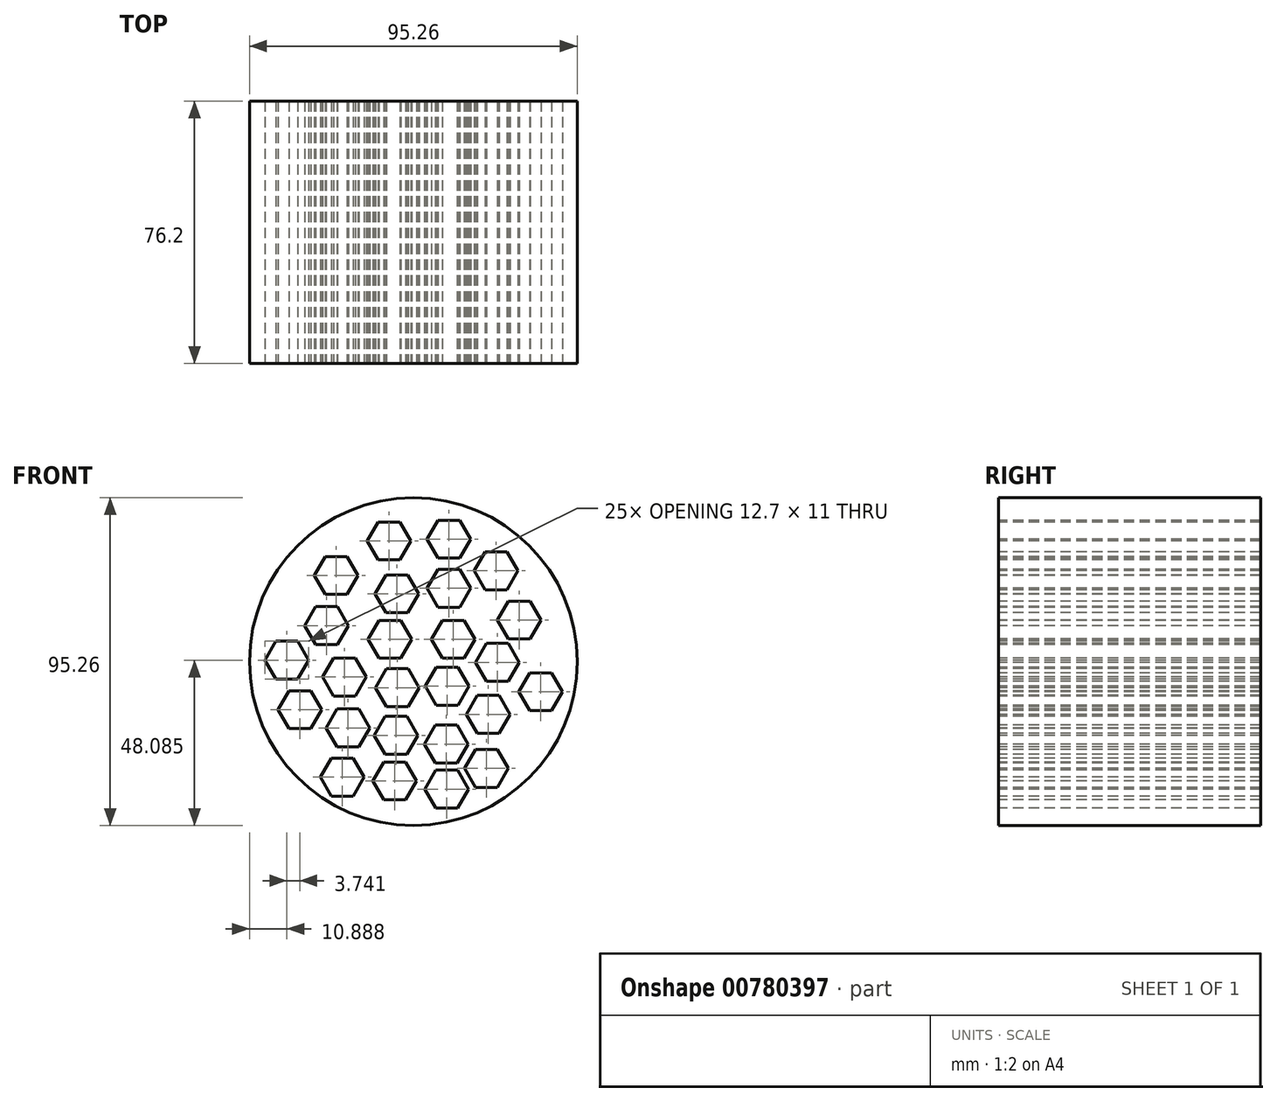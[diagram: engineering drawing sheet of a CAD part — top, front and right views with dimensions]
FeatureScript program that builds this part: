
annotation { "Feature Type Name" : "Feature", "Feature Type Description" : "" }
export const myFeature = defineFeature(function(context is Context, id is Id, definition is map)
    precondition{}
    {
        {
            var Q0;
            Q0=qCreatedBy(makeId("Front.planeOp"),FACE);
            var sketch = newSketch(context, id + "F0", { "sketchPlane" : qUnion([Q0])});
            skCircle(sketch, "E0", {"center": v(0, 0) * mm, "radius": 47.63 * mm});
            skSolve(sketch);
        }
        {
            var Q0;
            Q0=makeQuery(id+"F0.imprint","IMPRINT",FACE,{"disambiguationData":[TD([[makeQuery(id+"F0.imprint","IMPRINT",EDGE,{"derivedFrom":sQuery(id+"F0.wireOp",EDGE,"E0")}),1.0]])]});
            extrude(context, id + "F1", {"entities" : qUnion([Q0]), "depth" : 76.2 * mm, "offsetDistance" : 25.4 * mm});
        }
        {
            var Q0;
            Q0=makeQuery(id+"F1.opExtrude","CAP_FACE",FACE,{"disambiguationData":[OSD([sQuery(id+"F0.wireOp",EDGE,"E0")])],"isStart":false});
            var sketch = newSketch(context, id + "F2", { "sketchPlane" : qUnion([Q0])});
            skCircle(sketch, "E1.cCircle", {"center": v(-22.42, 25.02) * mm, "radius": 5.5 * mm, "construction": true});
            skLineSegment(sketch, "E1.0", {"start": v(-19.25, 30.52) * mm, "end": v(-16.07, 25.02) * mm});
            skLineSegment(sketch, "E1.1", {"start": v(-16.07, 25.02) * mm, "end": v(-19.25, 19.52) * mm});
            skLineSegment(sketch, "E1.2", {"start": v(-19.25, 19.52) * mm, "end": v(-25.6, 19.52) * mm});
            skLineSegment(sketch, "E1.3", {"start": v(-25.6, 19.52) * mm, "end": v(-28.77, 25.02) * mm});
            skLineSegment(sketch, "E1.4", {"start": v(-28.77, 25.02) * mm, "end": v(-25.6, 30.52) * mm});
            skLineSegment(sketch, "E1.5", {"start": v(-25.6, 30.52) * mm, "end": v(-19.25, 30.52) * mm});
            skPoint(sketch, "E1.0.midPoint", {"position": v(-17.66, 27.77) * mm});
            skCircle(sketch, "E2.cCircle", {"center": v(-7.08, 35.06) * mm, "radius": 5.5 * mm, "construction": true});
            skLineSegment(sketch, "E2.0", {"start": v(-3.9, 40.56) * mm, "end": v(-0.73, 35.06) * mm});
            skLineSegment(sketch, "E2.1", {"start": v(-0.73, 35.06) * mm, "end": v(-3.9, 29.56) * mm});
            skLineSegment(sketch, "E2.2", {"start": v(-3.9, 29.56) * mm, "end": v(-10.26, 29.56) * mm});
            skLineSegment(sketch, "E2.3", {"start": v(-10.26, 29.56) * mm, "end": v(-13.43, 35.06) * mm});
            skLineSegment(sketch, "E2.4", {"start": v(-13.43, 35.06) * mm, "end": v(-10.26, 40.56) * mm});
            skLineSegment(sketch, "E2.5", {"start": v(-10.26, 40.56) * mm, "end": v(-3.9, 40.56) * mm});
            skPoint(sketch, "E2.0.midPoint", {"position": v(-2.32, 37.8) * mm});
            skCircle(sketch, "E3.cCircle", {"center": v(10.28, 35.6) * mm, "radius": 5.5 * mm, "construction": true});
            skLineSegment(sketch, "E3.0", {"start": v(13.46, 41.09) * mm, "end": v(16.63, 35.6) * mm});
            skLineSegment(sketch, "E3.1", {"start": v(16.63, 35.6) * mm, "end": v(13.46, 30.1) * mm});
            skLineSegment(sketch, "E3.2", {"start": v(13.46, 30.1) * mm, "end": v(7.1, 30.1) * mm});
            skLineSegment(sketch, "E3.3", {"start": v(7.1, 30.1) * mm, "end": v(3.93, 35.6) * mm});
            skLineSegment(sketch, "E3.4", {"start": v(3.93, 35.6) * mm, "end": v(7.1, 41.09) * mm});
            skLineSegment(sketch, "E3.5", {"start": v(7.1, 41.09) * mm, "end": v(13.46, 41.09) * mm});
            skPoint(sketch, "E3.0.midPoint", {"position": v(15.05, 38.34) * mm});
            skCircle(sketch, "E4.cCircle", {"center": v(-4.81, 19.7) * mm, "radius": 5.5 * mm, "construction": true});
            skLineSegment(sketch, "E4.0", {"start": v(-1.64, 25.2) * mm, "end": v(1.54, 19.7) * mm});
            skLineSegment(sketch, "E4.1", {"start": v(1.54, 19.7) * mm, "end": v(-1.64, 14.2) * mm});
            skLineSegment(sketch, "E4.2", {"start": v(-1.64, 14.2) * mm, "end": v(-7.99, 14.2) * mm});
            skLineSegment(sketch, "E4.3", {"start": v(-7.99, 14.2) * mm, "end": v(-11.16, 19.7) * mm});
            skLineSegment(sketch, "E4.4", {"start": v(-11.16, 19.7) * mm, "end": v(-7.99, 25.2) * mm});
            skLineSegment(sketch, "E4.5", {"start": v(-7.99, 25.2) * mm, "end": v(-1.64, 25.2) * mm});
            skPoint(sketch, "E4.0.midPoint", {"position": v(-0.05, 22.44) * mm});
            skCircle(sketch, "E5.cCircle", {"center": v(10.28, 21.3) * mm, "radius": 5.5 * mm, "construction": true});
            skLineSegment(sketch, "E5.0", {"start": v(13.46, 26.8) * mm, "end": v(16.63, 21.3) * mm});
            skLineSegment(sketch, "E5.1", {"start": v(16.63, 21.3) * mm, "end": v(13.46, 15.8) * mm});
            skLineSegment(sketch, "E5.2", {"start": v(13.46, 15.8) * mm, "end": v(7.1, 15.8) * mm});
            skLineSegment(sketch, "E5.3", {"start": v(7.1, 15.8) * mm, "end": v(3.93, 21.3) * mm});
            skLineSegment(sketch, "E5.4", {"start": v(3.93, 21.3) * mm, "end": v(7.1, 26.8) * mm});
            skLineSegment(sketch, "E5.5", {"start": v(7.1, 26.8) * mm, "end": v(13.46, 26.8) * mm});
            skPoint(sketch, "E5.0.midPoint", {"position": v(15.05, 24.05) * mm});
            skCircle(sketch, "E6.cCircle", {"center": v(24.04, 26.37) * mm, "radius": 5.5 * mm, "construction": true});
            skLineSegment(sketch, "E6.0", {"start": v(27.22, 31.87) * mm, "end": v(30.4, 26.37) * mm});
            skLineSegment(sketch, "E6.1", {"start": v(30.4, 26.37) * mm, "end": v(27.22, 20.87) * mm});
            skLineSegment(sketch, "E6.2", {"start": v(27.22, 20.87) * mm, "end": v(20.87, 20.87) * mm});
            skLineSegment(sketch, "E6.3", {"start": v(20.87, 20.87) * mm, "end": v(17.7, 26.37) * mm});
            skLineSegment(sketch, "E6.4", {"start": v(17.7, 26.37) * mm, "end": v(20.87, 31.87) * mm});
            skLineSegment(sketch, "E6.5", {"start": v(20.87, 31.87) * mm, "end": v(27.22, 31.87) * mm});
            skPoint(sketch, "E6.0.midPoint", {"position": v(28.8, 29.12) * mm});
            skCircle(sketch, "E7.cCircle", {"center": v(30.72, 12.08) * mm, "radius": 5.5 * mm, "construction": true});
            skLineSegment(sketch, "E7.0", {"start": v(33.9, 17.58) * mm, "end": v(37.07, 12.08) * mm});
            skLineSegment(sketch, "E7.1", {"start": v(37.07, 12.08) * mm, "end": v(33.9, 6.58) * mm});
            skLineSegment(sketch, "E7.2", {"start": v(33.9, 6.58) * mm, "end": v(27.55, 6.58) * mm});
            skLineSegment(sketch, "E7.3", {"start": v(27.55, 6.58) * mm, "end": v(24.37, 12.08) * mm});
            skLineSegment(sketch, "E7.4", {"start": v(24.37, 12.08) * mm, "end": v(27.55, 17.58) * mm});
            skLineSegment(sketch, "E7.5", {"start": v(27.55, 17.58) * mm, "end": v(33.9, 17.58) * mm});
            skPoint(sketch, "E7.0.midPoint", {"position": v(35.49, 14.83) * mm});
            skCircle(sketch, "E8.cCircle", {"center": v(11.62, 6.47) * mm, "radius": 5.5 * mm, "construction": true});
            skLineSegment(sketch, "E8.0", {"start": v(14.8, 11.97) * mm, "end": v(17.97, 6.47) * mm});
            skLineSegment(sketch, "E8.1", {"start": v(17.97, 6.47) * mm, "end": v(14.8, 0.97) * mm});
            skLineSegment(sketch, "E8.2", {"start": v(14.8, 0.97) * mm, "end": v(8.44, 0.97) * mm});
            skLineSegment(sketch, "E8.3", {"start": v(8.44, 0.97) * mm, "end": v(5.27, 6.47) * mm});
            skLineSegment(sketch, "E8.4", {"start": v(5.27, 6.47) * mm, "end": v(8.44, 11.97) * mm});
            skLineSegment(sketch, "E8.5", {"start": v(8.44, 11.97) * mm, "end": v(14.8, 11.97) * mm});
            skPoint(sketch, "E8.0.midPoint", {"position": v(16.38, 9.22) * mm});
            skCircle(sketch, "E9.cCircle", {"center": v(-6.82, 6.47) * mm, "radius": 5.5 * mm, "construction": true});
            skLineSegment(sketch, "E9.0", {"start": v(-3.64, 11.97) * mm, "end": v(-0.47, 6.47) * mm});
            skLineSegment(sketch, "E9.1", {"start": v(-0.47, 6.47) * mm, "end": v(-3.64, 0.97) * mm});
            skLineSegment(sketch, "E9.2", {"start": v(-3.64, 0.97) * mm, "end": v(-10, 0.97) * mm});
            skLineSegment(sketch, "E9.3", {"start": v(-10, 0.97) * mm, "end": v(-13.17, 6.47) * mm});
            skLineSegment(sketch, "E9.4", {"start": v(-13.17, 6.47) * mm, "end": v(-10, 11.97) * mm});
            skLineSegment(sketch, "E9.5", {"start": v(-10, 11.97) * mm, "end": v(-3.64, 11.97) * mm});
            skPoint(sketch, "E9.0.midPoint", {"position": v(-2.05, 9.22) * mm});
            skCircle(sketch, "E10.cCircle", {"center": v(-25.25, 10.47) * mm, "radius": 5.5 * mm, "construction": true});
            skLineSegment(sketch, "E10.0", {"start": v(-22.08, 15.97) * mm, "end": v(-18.9, 10.47) * mm});
            skLineSegment(sketch, "E10.1", {"start": v(-18.9, 10.47) * mm, "end": v(-22.08, 4.98) * mm});
            skLineSegment(sketch, "E10.2", {"start": v(-22.08, 4.98) * mm, "end": v(-28.43, 4.98) * mm});
            skLineSegment(sketch, "E10.3", {"start": v(-28.43, 4.98) * mm, "end": v(-31.6, 10.47) * mm});
            skLineSegment(sketch, "E10.4", {"start": v(-31.6, 10.47) * mm, "end": v(-28.43, 15.97) * mm});
            skLineSegment(sketch, "E10.5", {"start": v(-28.43, 15.97) * mm, "end": v(-22.08, 15.97) * mm});
            skPoint(sketch, "E10.0.midPoint", {"position": v(-20.5, 13.22) * mm});
            skCircle(sketch, "E11.cCircle", {"center": v(-36.74, 0.46) * mm, "radius": 5.5 * mm, "construction": true});
            skLineSegment(sketch, "E11.0", {"start": v(-33.57, 5.95) * mm, "end": v(-30.4, 0.46) * mm});
            skLineSegment(sketch, "E11.1", {"start": v(-30.4, 0.46) * mm, "end": v(-33.57, -5.04) * mm});
            skLineSegment(sketch, "E11.2", {"start": v(-33.57, -5.04) * mm, "end": v(-39.92, -5.04) * mm});
            skLineSegment(sketch, "E11.3", {"start": v(-39.92, -5.04) * mm, "end": v(-43.1, 0.46) * mm});
            skLineSegment(sketch, "E11.4", {"start": v(-43.1, 0.46) * mm, "end": v(-39.92, 5.95) * mm});
            skLineSegment(sketch, "E11.5", {"start": v(-39.92, 5.95) * mm, "end": v(-33.57, 5.95) * mm});
            skPoint(sketch, "E11.0.midPoint", {"position": v(-31.98, 3.2) * mm});
            skCircle(sketch, "E12.cCircle", {"center": v(-33, -13.97) * mm, "radius": 5.5 * mm, "construction": true});
            skLineSegment(sketch, "E12.0", {"start": v(-29.83, -8.47) * mm, "end": v(-26.65, -13.97) * mm});
            skLineSegment(sketch, "E12.1", {"start": v(-26.65, -13.97) * mm, "end": v(-29.83, -19.47) * mm});
            skLineSegment(sketch, "E12.2", {"start": v(-29.83, -19.47) * mm, "end": v(-36.18, -19.47) * mm});
            skLineSegment(sketch, "E12.3", {"start": v(-36.18, -19.47) * mm, "end": v(-39.35, -13.97) * mm});
            skLineSegment(sketch, "E12.4", {"start": v(-39.35, -13.97) * mm, "end": v(-36.18, -8.47) * mm});
            skLineSegment(sketch, "E12.5", {"start": v(-36.18, -8.47) * mm, "end": v(-29.83, -8.47) * mm});
            skPoint(sketch, "E12.0.midPoint", {"position": v(-28.24, -11.22) * mm});
            skCircle(sketch, "E13.cCircle", {"center": v(-20.04, -4.49) * mm, "radius": 5.5 * mm, "construction": true});
            skLineSegment(sketch, "E13.0", {"start": v(-16.87, 1.01) * mm, "end": v(-13.7, -4.49) * mm});
            skLineSegment(sketch, "E13.1", {"start": v(-13.7, -4.49) * mm, "end": v(-16.87, -9.99) * mm});
            skLineSegment(sketch, "E13.2", {"start": v(-16.87, -9.99) * mm, "end": v(-23.22, -9.99) * mm});
            skLineSegment(sketch, "E13.3", {"start": v(-23.22, -9.99) * mm, "end": v(-26.4, -4.49) * mm});
            skLineSegment(sketch, "E13.4", {"start": v(-26.4, -4.49) * mm, "end": v(-23.22, 1.01) * mm});
            skLineSegment(sketch, "E13.5", {"start": v(-23.22, 1.01) * mm, "end": v(-16.87, 1.01) * mm});
            skPoint(sketch, "E13.0.midPoint", {"position": v(-15.28, -1.74) * mm});
            skCircle(sketch, "E14.cCircle", {"center": v(-4.68, -7.56) * mm, "radius": 5.5 * mm, "construction": true});
            skLineSegment(sketch, "E14.0", {"start": v(-1.5, -2.06) * mm, "end": v(1.67, -7.56) * mm});
            skLineSegment(sketch, "E14.1", {"start": v(1.67, -7.56) * mm, "end": v(-1.5, -13.06) * mm});
            skLineSegment(sketch, "E14.2", {"start": v(-1.5, -13.06) * mm, "end": v(-7.85, -13.06) * mm});
            skLineSegment(sketch, "E14.3", {"start": v(-7.85, -13.06) * mm, "end": v(-11.03, -7.56) * mm});
            skLineSegment(sketch, "E14.4", {"start": v(-11.03, -7.56) * mm, "end": v(-7.85, -2.06) * mm});
            skLineSegment(sketch, "E14.5", {"start": v(-7.85, -2.06) * mm, "end": v(-1.5, -2.06) * mm});
            skPoint(sketch, "E14.0.midPoint", {"position": v(0.08, -4.81) * mm});
            skCircle(sketch, "E15.cCircle", {"center": v(9.75, -7.16) * mm, "radius": 5.5 * mm, "construction": true});
            skLineSegment(sketch, "E15.0", {"start": v(12.92, -1.66) * mm, "end": v(16.1, -7.16) * mm});
            skLineSegment(sketch, "E15.1", {"start": v(16.1, -7.16) * mm, "end": v(12.92, -12.66) * mm});
            skLineSegment(sketch, "E15.2", {"start": v(12.92, -12.66) * mm, "end": v(6.57, -12.66) * mm});
            skLineSegment(sketch, "E15.3", {"start": v(6.57, -12.66) * mm, "end": v(3.4, -7.16) * mm});
            skLineSegment(sketch, "E15.4", {"start": v(3.4, -7.16) * mm, "end": v(6.57, -1.66) * mm});
            skLineSegment(sketch, "E15.5", {"start": v(6.57, -1.66) * mm, "end": v(12.92, -1.66) * mm});
            skPoint(sketch, "E15.0.midPoint", {"position": v(14.51, -4.4) * mm});
            skCircle(sketch, "E16.cCircle", {"center": v(24.44, -0.21) * mm, "radius": 5.5 * mm, "construction": true});
            skLineSegment(sketch, "E16.0", {"start": v(27.62, 5.29) * mm, "end": v(30.8, -0.21) * mm});
            skLineSegment(sketch, "E16.1", {"start": v(30.8, -0.21) * mm, "end": v(27.62, -5.71) * mm});
            skLineSegment(sketch, "E16.2", {"start": v(27.62, -5.71) * mm, "end": v(21.27, -5.71) * mm});
            skLineSegment(sketch, "E16.3", {"start": v(21.27, -5.71) * mm, "end": v(18.1, -0.21) * mm});
            skLineSegment(sketch, "E16.4", {"start": v(18.1, -0.21) * mm, "end": v(21.27, 5.29) * mm});
            skLineSegment(sketch, "E16.5", {"start": v(21.27, 5.29) * mm, "end": v(27.62, 5.29) * mm});
            skPoint(sketch, "E16.0.midPoint", {"position": v(29.2, 2.54) * mm});
            skCircle(sketch, "E17.cCircle", {"center": v(37, -8.76) * mm, "radius": 5.5 * mm, "construction": true});
            skLineSegment(sketch, "E17.0", {"start": v(40.18, -3.26) * mm, "end": v(43.35, -8.76) * mm});
            skLineSegment(sketch, "E17.1", {"start": v(43.35, -8.76) * mm, "end": v(40.18, -14.26) * mm});
            skLineSegment(sketch, "E17.2", {"start": v(40.18, -14.26) * mm, "end": v(33.83, -14.26) * mm});
            skLineSegment(sketch, "E17.3", {"start": v(33.83, -14.26) * mm, "end": v(30.65, -8.76) * mm});
            skLineSegment(sketch, "E17.4", {"start": v(30.65, -8.76) * mm, "end": v(33.83, -3.26) * mm});
            skLineSegment(sketch, "E17.5", {"start": v(33.83, -3.26) * mm, "end": v(40.18, -3.26) * mm});
            skPoint(sketch, "E17.0.midPoint", {"position": v(41.76, -6.01) * mm});
            skCircle(sketch, "E18.cCircle", {"center": v(21.77, -15.3) * mm, "radius": 5.5 * mm, "construction": true});
            skLineSegment(sketch, "E18.0", {"start": v(24.95, -9.8) * mm, "end": v(28.12, -15.3) * mm});
            skLineSegment(sketch, "E18.1", {"start": v(28.12, -15.3) * mm, "end": v(24.95, -20.8) * mm});
            skLineSegment(sketch, "E18.2", {"start": v(24.95, -20.8) * mm, "end": v(18.6, -20.8) * mm});
            skLineSegment(sketch, "E18.3", {"start": v(18.6, -20.8) * mm, "end": v(15.42, -15.3) * mm});
            skLineSegment(sketch, "E18.4", {"start": v(15.42, -15.3) * mm, "end": v(18.6, -9.8) * mm});
            skLineSegment(sketch, "E18.5", {"start": v(18.6, -9.8) * mm, "end": v(24.95, -9.8) * mm});
            skPoint(sketch, "E18.0.midPoint", {"position": v(26.53, -12.56) * mm});
            skCircle(sketch, "E19.cCircle", {"center": v(-19.04, -19.26) * mm, "radius": 5.5 * mm, "construction": true});
            skLineSegment(sketch, "E19.0", {"start": v(-15.86, -13.76) * mm, "end": v(-12.69, -19.26) * mm});
            skLineSegment(sketch, "E19.1", {"start": v(-12.69, -19.26) * mm, "end": v(-15.86, -24.76) * mm});
            skLineSegment(sketch, "E19.2", {"start": v(-15.86, -24.76) * mm, "end": v(-22.21, -24.76) * mm});
            skLineSegment(sketch, "E19.3", {"start": v(-22.21, -24.76) * mm, "end": v(-25.39, -19.26) * mm});
            skLineSegment(sketch, "E19.4", {"start": v(-25.39, -19.26) * mm, "end": v(-22.21, -13.76) * mm});
            skLineSegment(sketch, "E19.5", {"start": v(-22.21, -13.76) * mm, "end": v(-15.86, -13.76) * mm});
            skPoint(sketch, "E19.0.midPoint", {"position": v(-14.28, -16.5) * mm});
            skCircle(sketch, "E20.cCircle", {"center": v(-5.01, -21.4) * mm, "radius": 5.5 * mm, "construction": true});
            skLineSegment(sketch, "E20.0", {"start": v(-1.84, -15.9) * mm, "end": v(1.34, -21.4) * mm});
            skLineSegment(sketch, "E20.1", {"start": v(1.34, -21.4) * mm, "end": v(-1.84, -26.9) * mm});
            skLineSegment(sketch, "E20.2", {"start": v(-1.84, -26.9) * mm, "end": v(-8.19, -26.9) * mm});
            skLineSegment(sketch, "E20.3", {"start": v(-8.19, -26.9) * mm, "end": v(-11.36, -21.4) * mm});
            skLineSegment(sketch, "E20.4", {"start": v(-11.36, -21.4) * mm, "end": v(-8.19, -15.9) * mm});
            skLineSegment(sketch, "E20.5", {"start": v(-8.19, -15.9) * mm, "end": v(-1.84, -15.9) * mm});
            skPoint(sketch, "E20.0.midPoint", {"position": v(-0.25, -18.65) * mm});
            skCircle(sketch, "E21.cCircle", {"center": v(9.55, -23.93) * mm, "radius": 5.5 * mm, "construction": true});
            skLineSegment(sketch, "E21.0", {"start": v(12.73, -18.43) * mm, "end": v(15.9, -23.93) * mm});
            skLineSegment(sketch, "E21.1", {"start": v(15.9, -23.93) * mm, "end": v(12.73, -29.43) * mm});
            skLineSegment(sketch, "E21.2", {"start": v(12.73, -29.43) * mm, "end": v(6.38, -29.43) * mm});
            skLineSegment(sketch, "E21.3", {"start": v(6.38, -29.43) * mm, "end": v(3.2, -23.93) * mm});
            skLineSegment(sketch, "E21.4", {"start": v(3.2, -23.93) * mm, "end": v(6.38, -18.43) * mm});
            skLineSegment(sketch, "E21.5", {"start": v(6.38, -18.43) * mm, "end": v(12.73, -18.43) * mm});
            skPoint(sketch, "E21.0.midPoint", {"position": v(14.31, -21.18) * mm});
            skCircle(sketch, "E22.cCircle", {"center": v(-5.48, -34.68) * mm, "radius": 5.5 * mm, "construction": true});
            skLineSegment(sketch, "E22.0", {"start": v(-2.3, -29.18) * mm, "end": v(0.87, -34.68) * mm});
            skLineSegment(sketch, "E22.1", {"start": v(0.87, -34.68) * mm, "end": v(-2.3, -40.18) * mm});
            skLineSegment(sketch, "E22.2", {"start": v(-2.3, -40.18) * mm, "end": v(-8.66, -40.18) * mm});
            skLineSegment(sketch, "E22.3", {"start": v(-8.66, -40.18) * mm, "end": v(-11.83, -34.68) * mm});
            skLineSegment(sketch, "E22.4", {"start": v(-11.83, -34.68) * mm, "end": v(-8.66, -29.18) * mm});
            skLineSegment(sketch, "E22.5", {"start": v(-8.66, -29.18) * mm, "end": v(-2.3, -29.18) * mm});
            skPoint(sketch, "E22.0.midPoint", {"position": v(-0.72, -31.93) * mm});
            skCircle(sketch, "E23.cCircle", {"center": v(-20.64, -33.55) * mm, "radius": 5.5 * mm, "construction": true});
            skLineSegment(sketch, "E23.0", {"start": v(-17.47, -28.05) * mm, "end": v(-14.3, -33.55) * mm});
            skLineSegment(sketch, "E23.1", {"start": v(-14.3, -33.55) * mm, "end": v(-17.47, -39.05) * mm});
            skLineSegment(sketch, "E23.2", {"start": v(-17.47, -39.05) * mm, "end": v(-23.82, -39.05) * mm});
            skLineSegment(sketch, "E23.3", {"start": v(-23.82, -39.05) * mm, "end": v(-27, -33.55) * mm});
            skLineSegment(sketch, "E23.4", {"start": v(-27, -33.55) * mm, "end": v(-23.82, -28.05) * mm});
            skLineSegment(sketch, "E23.5", {"start": v(-23.82, -28.05) * mm, "end": v(-17.47, -28.05) * mm});
            skPoint(sketch, "E23.0.midPoint", {"position": v(-15.88, -30.8) * mm});
            skCircle(sketch, "E24.cCircle", {"center": v(21.17, -31.01) * mm, "radius": 5.5 * mm, "construction": true});
            skLineSegment(sketch, "E24.0", {"start": v(24.35, -25.51) * mm, "end": v(27.52, -31.01) * mm});
            skLineSegment(sketch, "E24.1", {"start": v(27.52, -31.01) * mm, "end": v(24.35, -36.51) * mm});
            skLineSegment(sketch, "E24.2", {"start": v(24.35, -36.51) * mm, "end": v(18, -36.51) * mm});
            skLineSegment(sketch, "E24.3", {"start": v(18, -36.51) * mm, "end": v(14.82, -31.01) * mm});
            skLineSegment(sketch, "E24.4", {"start": v(14.82, -31.01) * mm, "end": v(18, -25.51) * mm});
            skLineSegment(sketch, "E24.5", {"start": v(18, -25.51) * mm, "end": v(24.35, -25.51) * mm});
            skPoint(sketch, "E24.0.midPoint", {"position": v(25.94, -28.26) * mm});
            skCircle(sketch, "E25.cCircle", {"center": v(9.68, -37.03) * mm, "radius": 5.5 * mm, "construction": true});
            skLineSegment(sketch, "E25.0", {"start": v(12.86, -31.53) * mm, "end": v(16.03, -37.03) * mm});
            skLineSegment(sketch, "E25.1", {"start": v(16.03, -37.03) * mm, "end": v(12.86, -42.52) * mm});
            skLineSegment(sketch, "E25.2", {"start": v(12.86, -42.52) * mm, "end": v(6.5, -42.52) * mm});
            skLineSegment(sketch, "E25.3", {"start": v(6.5, -42.52) * mm, "end": v(3.33, -37.03) * mm});
            skLineSegment(sketch, "E25.4", {"start": v(3.33, -37.03) * mm, "end": v(6.5, -31.53) * mm});
            skLineSegment(sketch, "E25.5", {"start": v(6.5, -31.53) * mm, "end": v(12.86, -31.53) * mm});
            skPoint(sketch, "E25.0.midPoint", {"position": v(14.45, -34.28) * mm});
            skSolve(sketch);
        }
        {
            var Q0;
            Q0 = qSketchRegion(id + "F2", true);
            extrude(context, id + "F3", {"entities" : qUnion([Q0]), "operationType" : NewBodyOperationType.REMOVE, "endBound" : BoundingType.THROUGH_ALL, "oppositeDirection" : true, "depth" : 25.4 * mm, "offsetDistance" : 25.4 * mm});
        }
    });
